# Revit family: ISI_IdealStandard_WCPans_Concept_E7850
name_source: partatom
category: Plumbing Fixtures
revit_build: Autodesk Revit MEP 2012 (Build: 20110309_2315(x64)
units: mm (PartAtom-declared; Revit-internal decimal feet)

## types (1)
- E785001 - Concept wall mounted WC pan with horizontal outlet
    Accessories = www.idealspec.co.uk
    AreaUnits = millimeters
    Assembly Code = C1030200
    AssetType = Fixed
    BIMObjectName = ISI_IdealStandard_WCPans_Concept-WH_E7850
    Brand = Ideal Standard
    CWFU = 0
    Color = White
    ConnectionType = Plumbing
    Cost = 0 $
    Default Elevation = 400 mm  [stored 1.31234 ft]
    Description = Concept wall mounted wc pan with horizontal outlet
    DurationUnit = year
    ECA = Yes
    ExpectedLife = 30
    Features = Wall mounted wc pan with horizontal outlet
    Finish = White
    HWFU = 0
    Help = www.idealspec.co.uk/contact-us.html
    IfcExportAs = IfcSanitaryTerminalType
    IfcExportType = TOILETPAN
    InstallationInstructions = www.idealspec.co.uk/resources.html
    LinearUnits = millimeters
    ManufacturerURL = www.idealspec.co.uk
    Material = Vitreous china
    Model = E785001
    ModelNumber = E785001
    ModelReference = Concept wall mounted wc pan with horizontal outlet
    NBSDescription = WC pans
    NBSReference = 45-35-70/384
    Name = WCPans_ConceptWH_E7850_IdealStandard
    NettWeight = 24.6 Kg
    NominalDepth = 540 mm
    NominalHeight = 308 mm
    NominalLength = 540 mm
    NominalWidth = 360 mm
    PanColor = White
    PanMaterial = Vitreous china
    PanMounting = WallHung
    ProductInformation = www.idealspec.co.uk/assets/datasheet/E785001
    Shape = Sculptured
    Size = 360 x 540 x 308 mm
    Space = Internal
    SpareParts = www.fastpart-spares.co.uk
    SpilloverLevel = 0 mm  [stored 0 ft]
    ToiletPanType = WashDown
    ToiletType = Other
    URL = www.idealspec.co.uk
    Uniclass2 = Pr_40_20_93_94
    Version = 2
    VolumeUnits = Litres
    WFU = 0
    WRAS = No
    WarrantyDescription = Manufacturers Warranty
    WarrantyDurationParts = 99
    WarrantyDurationUnit = year
    WaterEfficientProduct = Yes

note: [stored X ft] marks values corroborated as IEEE doubles in the binary element streams (Revit-internal decimal feet)

## geometry (parser evidence)
native form markers: Blend x3, Sweep x10
no freeform markers — native parametric forms only
